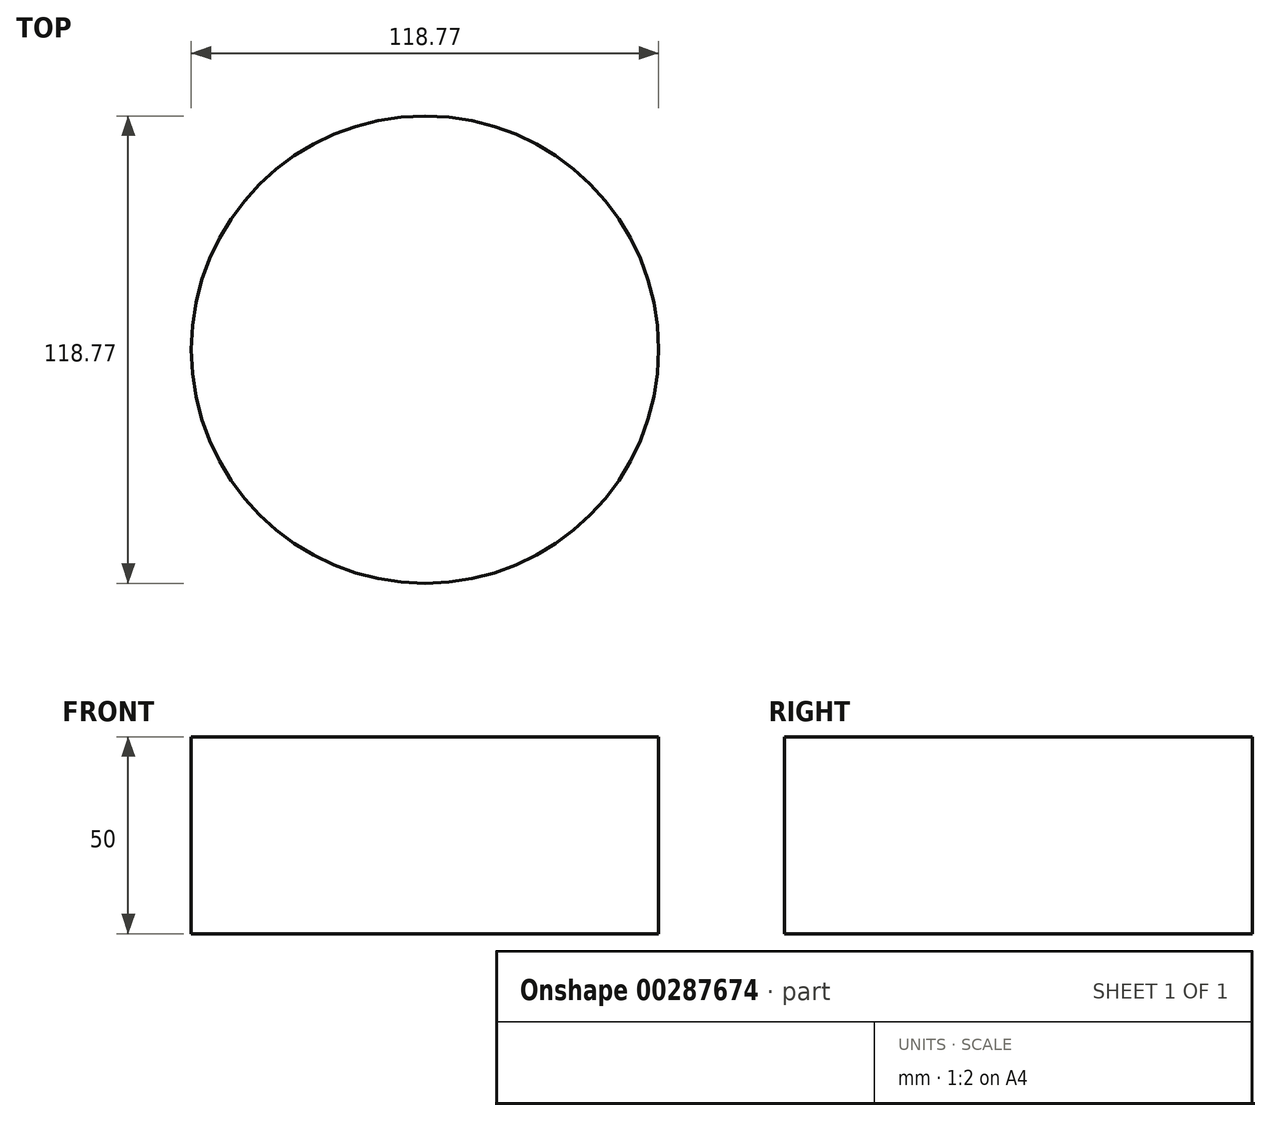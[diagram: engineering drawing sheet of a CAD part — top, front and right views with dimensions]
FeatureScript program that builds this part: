
annotation { "Feature Type Name" : "Feature", "Feature Type Description" : "" }
export const myFeature = defineFeature(function(context is Context, id is Id, definition is map)
    precondition{}
    {
        {
            var Q0;
            Q0=qCreatedBy(makeId("Top.planeOp"),FACE);
            var sketch = newSketch(context, id + "F0", { "sketchPlane" : qUnion([Q0])});
            skCircle(sketch, "E0", {"center": v(-0.85, -1.47) * mm, "radius": 59.39 * mm});
            skSolve(sketch);
        }
        {
            var Q0;
            Q0=makeQuery(id+"F0.imprint","IMPRINT",FACE,{"disambiguationData":[TD([[makeQuery(id+"F0.imprint","IMPRINT",EDGE,{"derivedFrom":sQuery(id+"F0.wireOp",EDGE,"E0")}),1.0]])]});
            extrude(context, id + "F1", {"entities" : qUnion([Q0]), "depth" : 50 * mm});
        }
    });
